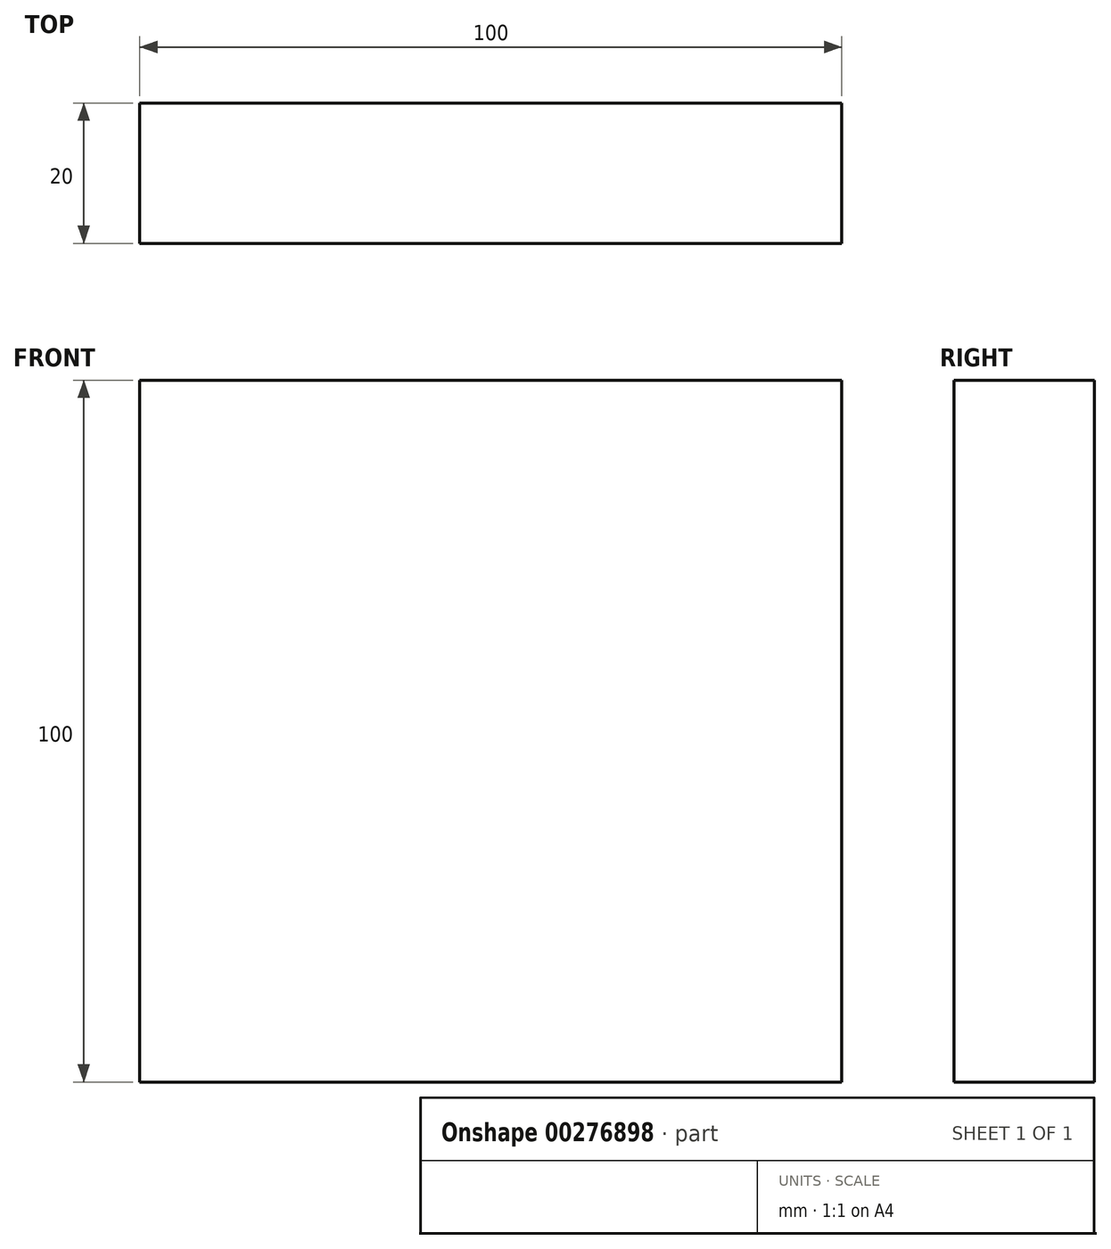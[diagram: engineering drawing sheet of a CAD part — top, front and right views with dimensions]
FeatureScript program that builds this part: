
annotation { "Feature Type Name" : "Feature", "Feature Type Description" : "" }
export const myFeature = defineFeature(function(context is Context, id is Id, definition is map)
    precondition{}
    {
        {
            var Q0;
            Q0=qCreatedBy(makeId("Front.planeOp"),FACE);
            var sketch = newSketch(context, id + "F0", { "sketchPlane" : qUnion([Q0])});
            skLineSegment(sketch, "E0.bottom", {"start": v(40.32, 105.8) * mm, "end": v(-59.68, 105.8) * mm});
            skLineSegment(sketch, "E0.top", {"start": v(40.32, 5.8) * mm, "end": v(-59.68, 5.8) * mm});
            skLineSegment(sketch, "E0.left", {"start": v(40.32, 105.8) * mm, "end": v(40.32, 5.8) * mm});
            skLineSegment(sketch, "E0.right", {"start": v(-59.68, 105.8) * mm, "end": v(-59.68, 5.8) * mm});
            skSolve(sketch);
        }
        {
            var Q0;
            Q0=makeQuery(id+"F0.imprint","IMPRINT",FACE,{"disambiguationData":[TD([[makeQuery(id+"F0.imprint","IMPRINT",EDGE,{"derivedFrom":sQuery(id+"F0.wireOp",EDGE,"E0.bottom")}),1.0]])]});
            extrude(context, id + "F1", {"entities" : qUnion([Q0]), "depth" : 20 * mm});
        }
    });
